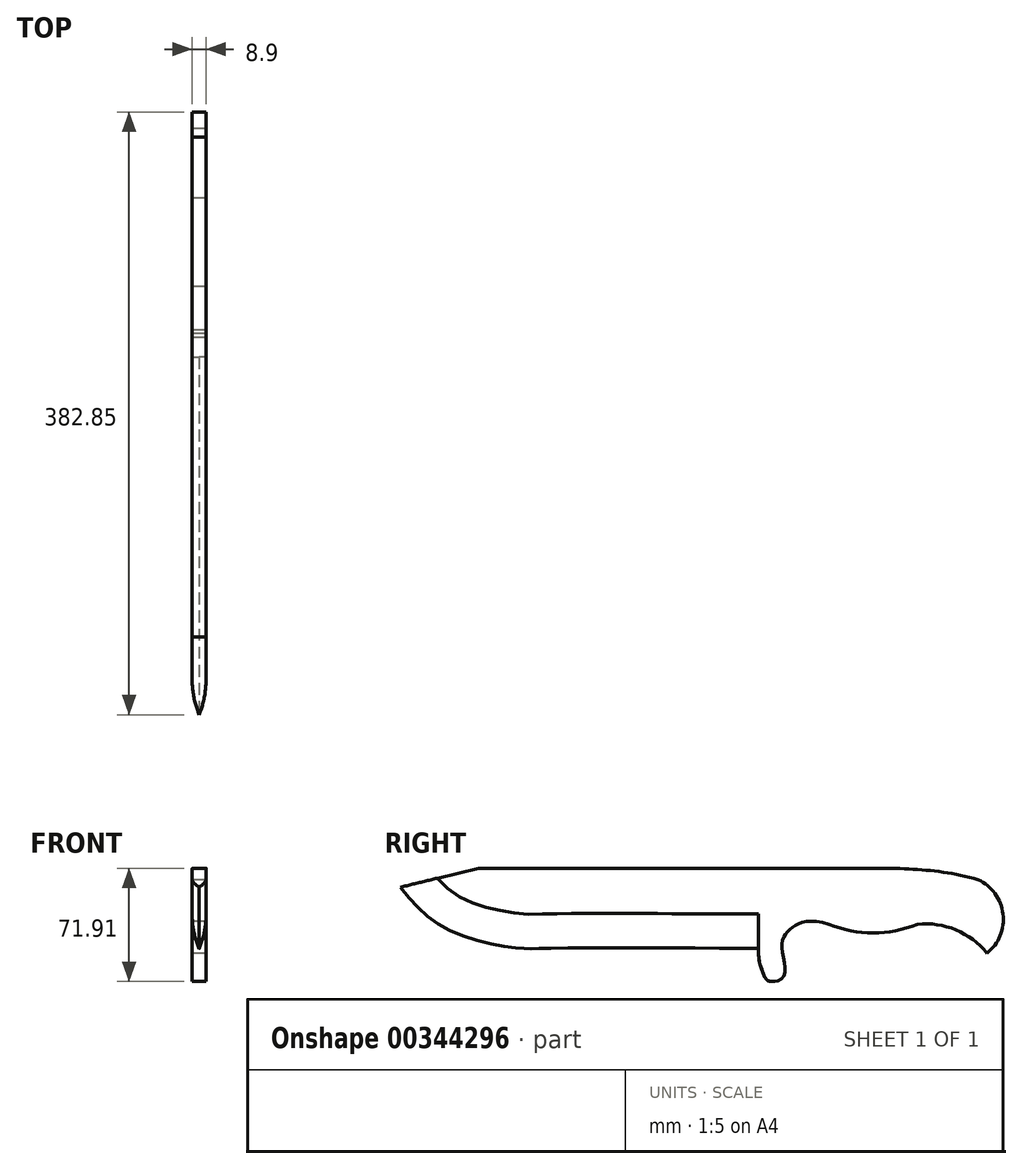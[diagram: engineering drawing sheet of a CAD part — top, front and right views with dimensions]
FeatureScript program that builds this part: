
annotation { "Feature Type Name" : "Feature", "Feature Type Description" : "" }
export const myFeature = defineFeature(function(context is Context, id is Id, definition is map)
    precondition{}
    {
        {
            var Q0;
            Q0=qCreatedBy(makeId("Right.planeOp"),FACE);
            var sketch = newSketch(context, id + "F0", { "sketchPlane" : qUnion([Q0])});
            skLineSegment(sketch, "E0", {"start": v(0, 0) * mm, "end": v(-177.8, 0) * mm});
            skLineSegment(sketch, "E1", {"start": v(-177.8, 0) * mm, "end": v(-227.17, -11.97) * mm});
            skLineSegment(sketch, "E2", {"start": v(0, 0) * mm, "end": v(0, -50.8) * mm});
            skLineSegment(sketch, "E3", {"start": v(0, 0) * mm, "end": v(76.2, 0) * mm});
            skArc(sketch, "E4", {"start": v(44.92, -35.5) * mm, "mid": v(72.98, -41.07) * mm, "end": v(101.05, -35.5) * mm});
            skArc(sketch, "E5", {"start": v(145.3, -53.97) * mm, "mid": v(155.49, -29.04) * mm, "end": v(139.68, -7.23) * mm});
            skArc(sketch, "E6", {"start": v(145.3, -53.97) * mm, "mid": v(125.53, -39.1) * mm, "end": v(101.05, -35.5) * mm});
            skFitSpline(sketch, "E7", {"points": [v(12.4, -71.52) * mm, v(15.1, -50.54) * mm, v(20.67, -38.25) * mm, v(44.92, -35.5) * mm], "startDerivative": vector(70.56, 17.64) * mm, "endDerivative": vector(103.84, -32.33) * mm});
            skFitSpline(sketch, "E8", {"points": [v(0, -50.8) * mm, v(2.55, -65.1) * mm, v(4.95, -70.3) * mm, v(12.4, -71.52) * mm], "startDerivative": vector(0, -51.84) * mm, "endDerivative": vector(43.65, 8.5) * mm});
            skFitSpline(sketch, "E9", {"points": [v(76.2, 0) * mm, v(139.68, -7.23) * mm], "startDerivative": vector(64.82, 0) * mm, "endDerivative": vector(64.8, -18.43) * mm});
            skFitSpline(sketch, "E10", {"points": [v(0, -50.8) * mm, v(-132.77, -50.8) * mm, v(-151.56, -50.8) * mm, v(-194.32, -40.22) * mm, v(-227.17, -11.97) * mm], "startDerivative": vector(-210.63, -0.03) * mm, "endDerivative": vector(-120.21, 162.87) * mm});
            skSolve(sketch);
        }
        {
            var Q0;
            {var subQ1=sQuery(id+"F0.wireOp",EDGE,"E0");Q0=makeQuery(id+"F0.imprint","IMPRINT",FACE,{"disambiguationData":[TD([[makeQuery(id+"F0.imprint","IMPRINT",EDGE,{"derivedFrom":subQ1}),1.0]])]});}
            var Q1;
            {var subQ3=sQuery(id+"F0.wireOp",EDGE,"JW7DoDEv-w5D9-3Zfo-a3na-f8gO57aVABPA");Q1=makeQuery(id+"F0.imprint","IMPRINT",FACE,{"disambiguationData":[TD([[makeQuery(id+"F0.imprint","IMPRINT",EDGE,{"derivedFrom":subQ3}),1.0]])]});}
            var Q2;
            {var subQ0=sQuery(id+"F0.wireOp",EDGE,"E3");Q2=makeQuery(id+"F0.imprint","IMPRINT",FACE,{"disambiguationData":[TD([[makeQuery(id+"F0.imprint","IMPRINT",EDGE,{"derivedFrom":subQ0}),-1.0]])]});}
            extrude(context, id + "F1", {"entities" : qUnion([Q0, Q1, Q2]), "depth" : 4.44 * mm});
        }
        {
            var Q0;
            Q0=makeQuery(id+"F1.opExtrude","CAP_EDGE",EDGE,{"disambiguationData":[OSD([sQuery(id+"F0.wireOp",EDGE,"E10")])],"isStart":false});
            fillet(context, id + "F2", {"entities" : qUnion([Q0]), "radius" : 55.8 * mm, "tangentPropagation" : true, "allowEdgeOverflow" : false});
        }
        {
            var Q0;
            Q0=makeQuery(id+"F1.opExtrude","SWEPT_BODY",BODY,{"disambiguationData":[OSD([sQuery(id+"F0.wireOp",EDGE,"E0"),sQuery(id+"F0.wireOp",EDGE,"E1"),sQuery(id+"F0.wireOp",EDGE,"E3"),sQuery(id+"F0.wireOp",EDGE,"E4"),sQuery(id+"F0.wireOp",EDGE,"E5"),sQuery(id+"F0.wireOp",EDGE,"E6"),sQuery(id+"F0.wireOp",EDGE,"E7"),sQuery(id+"F0.wireOp",EDGE,"E8"),sQuery(id+"F0.wireOp",EDGE,"E9"),sQuery(id+"F0.wireOp",EDGE,"E10")])]});
            var Q1;
            Q1=qCreatedBy(makeId("Right.planeOp"),FACE);
            mirror(context, id + "F3", {"operationType" : NewBodyOperationType.ADD, "entities" : qUnion([Q0]), "mirrorPlane" : qUnion([Q1])});
        }
    });
